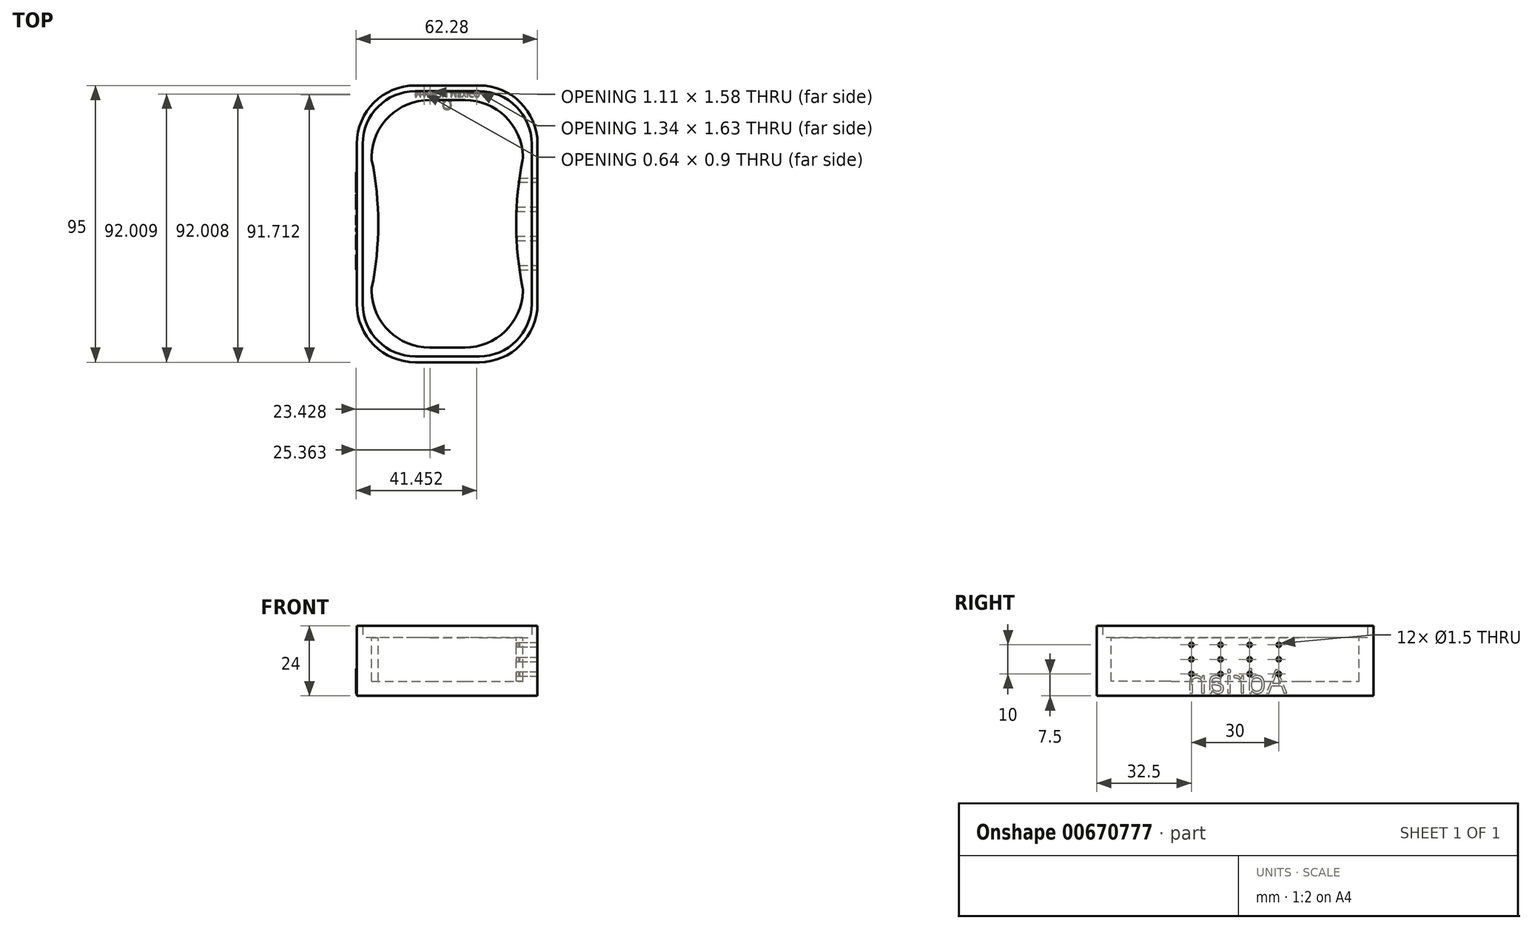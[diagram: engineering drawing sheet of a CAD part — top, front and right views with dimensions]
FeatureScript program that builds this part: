
annotation { "Feature Type Name" : "Feature", "Feature Type Description" : "" }
export const myFeature = defineFeature(function(context is Context, id is Id, definition is map)
    precondition{}
    {
        {
            var Q0;
            Q0=qCreatedBy(makeId("Top.planeOp"),FACE);
            var sketch = newSketch(context, id + "F0", { "sketchPlane" : qUnion([Q0])});
            skLineSegment(sketch, "E0", {"start": v(-100, 0) * mm, "end": v(100, 0) * mm, "construction": true});
            skLineSegment(sketch, "E1", {"start": v(0, 100) * mm, "end": v(0, 65) * mm, "construction": true});
            skLineSegment(sketch, "E2.bottom", {"start": v(20, 0) * mm, "end": v(32, 0) * mm});
            skLineSegment(sketch, "E2.top", {"start": v(20, 85) * mm, "end": v(32, 85) * mm});
            skPoint(sketch, "E3.visualSharp", {"position": v(0, 85) * mm});
            skArc(sketch, "E3.filletArc", {"start": v(20, 85) * mm, "mid": v(6.08, 79.36) * mm, "end": v(0, 65.63) * mm});
            skPoint(sketch, "E4.visualSharp", {"position": v(52, 85) * mm});
            skArc(sketch, "E4.filletArc", {"start": v(52, 65.63) * mm, "mid": v(45.92, 79.36) * mm, "end": v(32, 85) * mm});
            skPoint(sketch, "E5.visualSharp", {"position": v(52, 0) * mm});
            skArc(sketch, "E5.filletArc", {"start": v(32, 0) * mm, "mid": v(45.92, 5.64) * mm, "end": v(52, 19.37) * mm});
            skPoint(sketch, "E6.visualSharp", {"position": v(0, 0) * mm});
            skArc(sketch, "E6.filletArc", {"start": v(0, 19.37) * mm, "mid": v(6.08, 5.64) * mm, "end": v(20, 0) * mm});
            skArc(sketch, "E7", {"start": v(51.9, 64.48) * mm, "mid": v(49.67, 42.5) * mm, "end": v(51.9, 20.52) * mm});
            skArc(sketch, "E8", {"start": v(0.1, 20.52) * mm, "mid": v(2.33, 42.5) * mm, "end": v(0.1, 64.48) * mm});
            skLineSegment(sketch, "E9.trimOffspring", {"start": v(0, 20) * mm, "end": v(0, -100) * mm, "construction": true});
            skLineSegment(sketch, "E10", {"start": v(0, 65) * mm, "end": v(0, 20) * mm, "construction": true});
            skPoint(sketch, "E11.visualSharp", {"position": v(52, 20) * mm});
            skArc(sketch, "E11.filletArc", {"start": v(52, 19.37) * mm, "mid": v(51.97, 19.95) * mm, "end": v(51.9, 20.52) * mm});
            skPoint(sketch, "E12.visualSharp", {"position": v(0, 20) * mm});
            skArc(sketch, "E12.filletArc", {"start": v(0.1, 20.52) * mm, "mid": v(0.03, 19.95) * mm, "end": v(0, 19.37) * mm});
            skPoint(sketch, "E13.visualSharp", {"position": v(0, 65) * mm});
            skArc(sketch, "E13.filletArc", {"start": v(0, 65.63) * mm, "mid": v(0.03, 65.05) * mm, "end": v(0.1, 64.48) * mm});
            skPoint(sketch, "E14.visualSharp", {"position": v(52, 65) * mm});
            skArc(sketch, "E14.filletArc", {"start": v(51.9, 64.48) * mm, "mid": v(51.97, 65.05) * mm, "end": v(52, 65.63) * mm});
            skSolve(sketch);
        }
        {
            var Q0;
            Q0 = qSketchRegion(id + "F0", true);
            extrude(context, id + "F1", {"entities" : qUnion([Q0]), "oppositeDirection" : true, "depth" : 15 * mm, "offsetDistance" : 25 * mm});
        }
        {
            var Q0;
            Q0=qCreatedBy(makeId("Top.planeOp"),FACE);
            cPlane(context, id + "F2", {"entities" : qUnion([Q0]), "cplaneType" : CPlaneType.OFFSET, "offset" : 20 * mm, "oppositeDirection" : true, "width" : 150 * mm, "height" : 150 * mm});
        }
        {
            var Q0;
            Q0=qCreatedBy(id+"F2.planeOp",FACE);
            var sketch = newSketch(context, id + "F3", { "sketchPlane" : qUnion([Q0])});
            skLineSegment(sketch, "E15.bottom", {"start": v(-5, 90) * mm, "end": v(57, 90) * mm});
            skLineSegment(sketch, "E15.top", {"start": v(-5, -5) * mm, "end": v(57, -5) * mm});
            skLineSegment(sketch, "E15.left", {"start": v(-5, 90) * mm, "end": v(-5, -5) * mm});
            skLineSegment(sketch, "E15.right", {"start": v(57, 90) * mm, "end": v(57, -5) * mm});
            skSolve(sketch);
        }
        {
            var Q0;
            Q0 = qSketchRegion(id + "F3", true);
            extrude(context, id + "F4", {"entities" : qUnion([Q0]), "depth" : 20 * mm, "offsetDistance" : 25 * mm});
        }
        {
            var Q0;
            Q0=makeQuery(id+"F1.opExtrude","SWEPT_BODY",BODY,{"disambiguationData":[OSD([sQuery(id+"F0.wireOp",EDGE,"E2.bottom"),sQuery(id+"F0.wireOp",EDGE,"E2.top"),sQuery(id+"F0.wireOp",EDGE,"E3.filletArc"),sQuery(id+"F0.wireOp",EDGE,"E4.filletArc"),sQuery(id+"F0.wireOp",EDGE,"E5.filletArc"),sQuery(id+"F0.wireOp",EDGE,"E6.filletArc"),sQuery(id+"F0.wireOp",EDGE,"E7"),sQuery(id+"F0.wireOp",EDGE,"E8"),sQuery(id+"F0.wireOp",EDGE,"E11.filletArc"),sQuery(id+"F0.wireOp",EDGE,"E12.filletArc"),sQuery(id+"F0.wireOp",EDGE,"E13.filletArc"),sQuery(id+"F0.wireOp",EDGE,"E14.filletArc")])]});
            var Q1;
            Q1=makeQuery(id+"F4.opExtrude","SWEPT_BODY",BODY,{"disambiguationData":[OSD([sQuery(id+"F3.wireOp",EDGE,"E15.bottom"),sQuery(id+"F3.wireOp",EDGE,"E15.top"),sQuery(id+"F3.wireOp",EDGE,"E15.left"),sQuery(id+"F3.wireOp",EDGE,"E15.right")])]});
            booleanBodies(context, id + "F5", {"operationType" : BooleanOperationType.SUBTRACTION, "tools" : qUnion([Q0]), "targets" : qUnion([Q1])});
        }
        {
            var Q0;
            Q0=makeQuery(id+"F4.opExtrude","SWEPT_EDGE",EDGE,{"disambiguationData":[OSD([sQuery(id+"F3.wireOp",EDGE,"E15.top"),sQuery(id+"F3.wireOp",EDGE,"E15.left")])]});
            var Q1;
            Q1=makeQuery(id+"F4.opExtrude","SWEPT_EDGE",EDGE,{"disambiguationData":[OSD([sQuery(id+"F3.wireOp",EDGE,"E15.bottom"),sQuery(id+"F3.wireOp",EDGE,"E15.left")])]});
            var Q2;
            Q2=makeQuery(id+"F4.opExtrude","SWEPT_EDGE",EDGE,{"disambiguationData":[OSD([sQuery(id+"F3.wireOp",EDGE,"E15.bottom"),sQuery(id+"F3.wireOp",EDGE,"E15.right")])]});
            var Q3;
            Q3=makeQuery(id+"F4.opExtrude","SWEPT_EDGE",EDGE,{"disambiguationData":[OSD([sQuery(id+"F3.wireOp",EDGE,"E15.top"),sQuery(id+"F3.wireOp",EDGE,"E15.right")])]});
            fillet(context, id + "F6", {"entities" : qUnion([Q0, Q1, Q2, Q3]), "radius" : 20 * mm, "tangentPropagation" : true, "allowEdgeOverflow" : false});
        }
        {
            var Q0;
            Q0=makeQuery(id+"F4.opExtrude","SWEPT_FACE",FACE,{"disambiguationData":[OSD([sQuery(id+"F3.wireOp",EDGE,"E15.left")])]});
            var sketch = newSketch(context, id + "F7", { "sketchPlane" : qUnion([Q0])});
            skText(sketch, "E16", { "text": "Adrian\n", "fontName": "OpenSans-Regular.ttf"});
            const initialGuessF7  = {"E16": [-0.06024, -0.0191, 1, 0, 0.008]};
            skSetInitialGuess(sketch, initialGuessF7);
            skSolve(sketch);
        }
        {
            var Q0;
            Q0 = qSketchRegion(id + "F7", true);
            extrude(context, id + "F8", {"entities" : qUnion([Q0]), "operationType" : NewBodyOperationType.ADD, "depth" : .3 * mm, "offsetDistance" : 25 * mm});
        }
        {
            var Q0;
            Q0=makeQuery(id+"F4.opExtrude","CAP_FACE",FACE,{"disambiguationData":[OSD([sQuery(id+"F3.wireOp",EDGE,"E15.bottom"),sQuery(id+"F3.wireOp",EDGE,"E15.top"),sQuery(id+"F3.wireOp",EDGE,"E15.left"),sQuery(id+"F3.wireOp",EDGE,"E15.right")])],"isStart":true});
            var sketch = newSketch(context, id + "F9", { "sketchPlane" : qUnion([Q0])});
            skText(sketch, "E17", { "text": "MADE IN MEXICO\n", "fontName": "OpenSans-Regular.ttf"});
            skText(sketch, "E18", { "text": "Ω", "fontName": "OpenSans-Regular.ttf"});
            skLineSegment(sketch, "E19", {"start": v(-5, -70) * mm, "end": v(57, -70) * mm, "construction": true});
            skLineSegment(sketch, "E20", {"start": v(26, -90) * mm, "end": v(26, -70) * mm, "construction": true});
            skLineSegment(sketch, "E21", {"start": v(26, -90) * mm, "end": v(26, -88) * mm, "construction": true});
            skLineSegment(sketch, "E22", {"start": v(26.01, -85) * mm, "end": v(26, -86) * mm, "construction": true});
            const initialGuessF9  = {"E17": [0.01475, -0.088, 1, 0, 0.002], "E18": [0.02415, -0.085, 1, 0, 0.0033]};
            skSetInitialGuess(sketch, initialGuessF9);
            skSolve(sketch);
        }
        {
            var Q0;
            Q0 = qSketchRegion(id + "F9", true);
            extrude(context, id + "F10", {"entities" : qUnion([Q0]), "oppositeDirection" : true, "depth" : .2 * mm, "offsetDistance" : 25 * mm});
        }
        {
            var Q0;
            Q0=makeQuery(id+"F4.opExtrude","SWEPT_FACE",FACE,{"disambiguationData":[OSD([sQuery(id+"F3.wireOp",EDGE,"E15.right")])]});
            var sketch = newSketch(context, id + "F11", { "sketchPlane" : qUnion([Q0])});
            skCircle(sketch, "E23", {"center": v(27.5, -12.5) * mm, "radius": 0.75 * mm});
            skCircle(sketch, "E24.0.1.0", {"center": v(27.5, -7.5) * mm, "radius": 0.75 * mm});
            skCircle(sketch, "E24.0.2.0", {"center": v(27.5, -2.5) * mm, "radius": 0.75 * mm});
            skCircle(sketch, "E24.1.0.0", {"center": v(37.5, -12.5) * mm, "radius": 0.75 * mm});
            skCircle(sketch, "E24.1.1.0", {"center": v(37.5, -7.5) * mm, "radius": 0.75 * mm});
            skCircle(sketch, "E24.1.2.0", {"center": v(37.5, -2.5) * mm, "radius": 0.75 * mm});
            skCircle(sketch, "E24.2.0.0", {"center": v(47.5, -12.5) * mm, "radius": 0.75 * mm});
            skCircle(sketch, "E24.2.1.0", {"center": v(47.5, -7.5) * mm, "radius": 0.75 * mm});
            skCircle(sketch, "E24.2.2.0", {"center": v(47.5, -2.5) * mm, "radius": 0.75 * mm});
            skCircle(sketch, "E24.3.0.0", {"center": v(57.5, -12.5) * mm, "radius": 0.75 * mm});
            skCircle(sketch, "E24.3.1.0", {"center": v(57.5, -7.5) * mm, "radius": 0.75 * mm});
            skCircle(sketch, "E24.3.2.0", {"center": v(57.5, -2.5) * mm, "radius": 0.75 * mm});
            skLineSegment(sketch, "E24.direction1", {"start": v(27.5, -12.5) * mm, "end": v(37.5, -12.5) * mm, "construction": true});
            skLineSegment(sketch, "E24.direction2", {"start": v(27.5, -12.5) * mm, "end": v(27.5, -7.5) * mm, "construction": true});
            skSolve(sketch);
        }
        {
            var Q0;
            Q0 = qSketchRegion(id + "F11", true);
            extrude(context, id + "F12", {"entities" : qUnion([Q0]), "operationType" : NewBodyOperationType.REMOVE, "oppositeDirection" : true, "depth" : 25 * mm, "offsetDistance" : 25 * mm});
        }
        {
            var Q0;
            Q0=makeQuery(id+"F4.opExtrude","CAP_FACE",FACE,{"disambiguationData":[OSD([sQuery(id+"F3.wireOp",EDGE,"E15.bottom"),sQuery(id+"F3.wireOp",EDGE,"E15.top"),sQuery(id+"F3.wireOp",EDGE,"E15.left"),sQuery(id+"F3.wireOp",EDGE,"E15.right")])],"isStart":false});
            var sketch = newSketch(context, id + "F13", { "sketchPlane" : qUnion([Q0])});
            skArc(sketch, "E25.0", {"start": v(15, 88) * mm, "mid": v(2.28, 82.73) * mm, "end": v(-3, 70) * mm});
            skLineSegment(sketch, "E25.1", {"start": v(37, 88) * mm, "end": v(15, 88) * mm});
            skLineSegment(sketch, "E25.2", {"start": v(-3, 70) * mm, "end": v(-3, 15) * mm});
            skArc(sketch, "E25.3", {"start": v(55, 70) * mm, "mid": v(49.72, 82.73) * mm, "end": v(37, 88) * mm});
            skArc(sketch, "E25.4", {"start": v(-3, 15) * mm, "mid": v(2.28, 2.27) * mm, "end": v(15, -3) * mm});
            skLineSegment(sketch, "E25.5", {"start": v(15, -3) * mm, "end": v(37, -3) * mm});
            skArc(sketch, "E25.6", {"start": v(37, -3) * mm, "mid": v(49.72, 2.27) * mm, "end": v(55, 15) * mm});
            skLineSegment(sketch, "E25.7", {"start": v(55, 15) * mm, "end": v(55, 70) * mm});
            skSolve(sketch);
        }
        {
            var Q0;
            Q0=makeQuery(id+"F13.imprint","IMPRINT",FACE,{"disambiguationData":[TD([[makeQuery(id+"F13.imprint","IMPRINT",EDGE,{"derivedFrom":sQuery(id+"F13.wireOp",EDGE,"E25.0")}),-1.0]])]});
            extrude(context, id + "F14", {"entities" : qUnion([Q0]), "operationType" : NewBodyOperationType.ADD, "depth" : 4 * mm, "offsetDistance" : 25 * mm});
        }
    });
